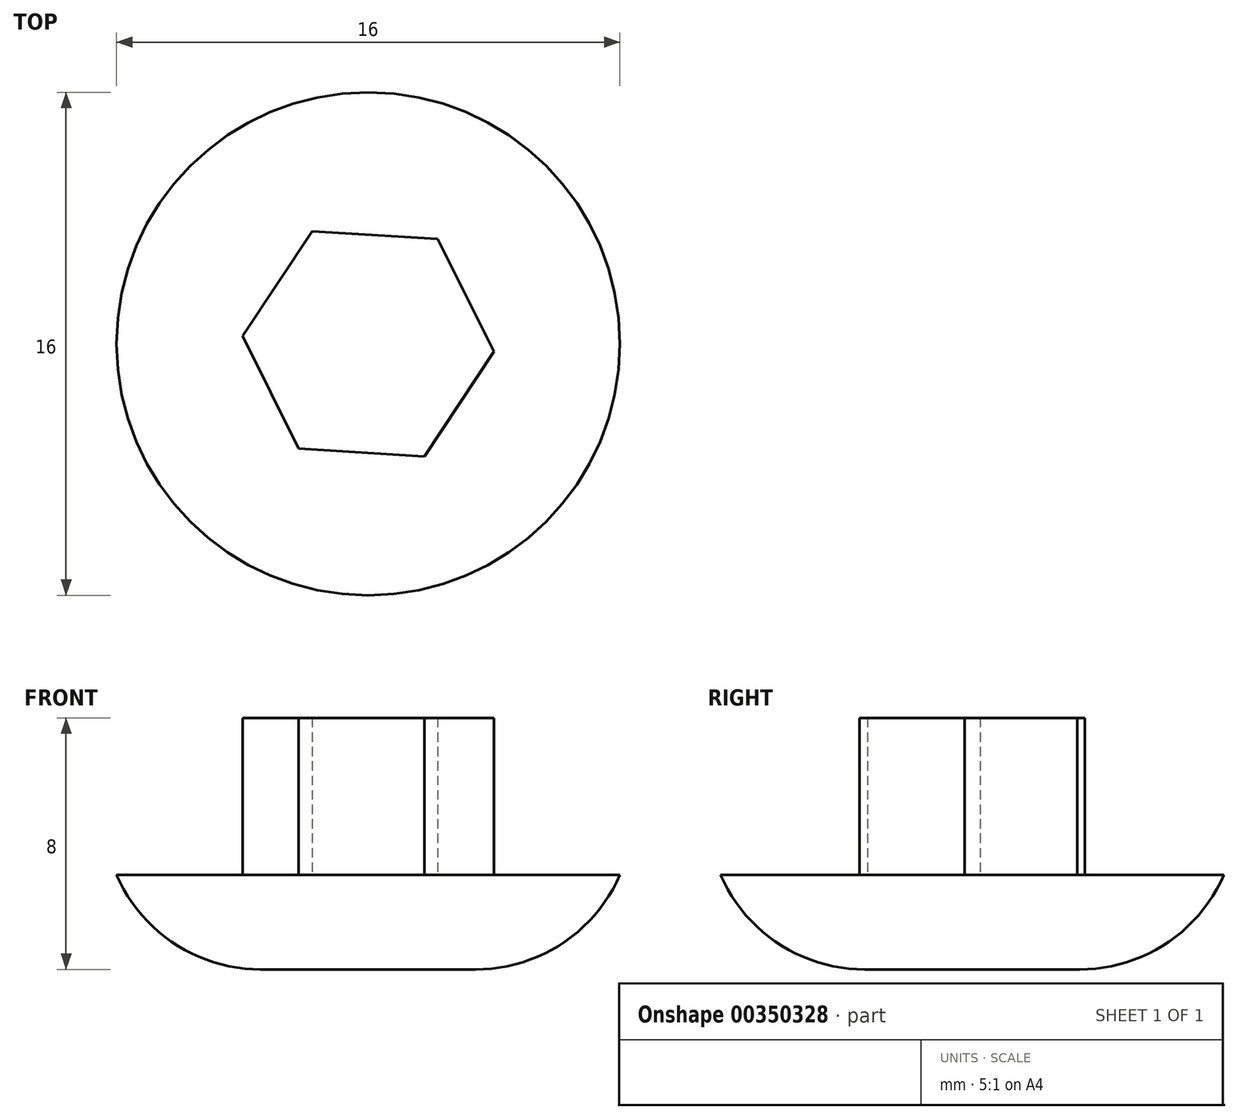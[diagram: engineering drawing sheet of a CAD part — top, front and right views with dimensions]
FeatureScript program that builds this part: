
annotation { "Feature Type Name" : "Feature", "Feature Type Description" : "" }
export const myFeature = defineFeature(function(context is Context, id is Id, definition is map)
    precondition{}
    {
        {
            var Q0;
            Q0=qCreatedBy(makeId("Top.planeOp"),FACE);
            var sketch = newSketch(context, id + "F0", { "sketchPlane" : qUnion([Q0])});
            skCircle(sketch, "E0.cCircle", {"center": v(0.6, 0) * mm, "radius": 3.46 * mm, "construction": true});
            skLineSegment(sketch, "E0.0", {"start": v(2.81, 3.33) * mm, "end": v(4.6, -0.25) * mm});
            skLineSegment(sketch, "E0.1", {"start": v(4.6, -0.25) * mm, "end": v(2.38, -3.58) * mm});
            skLineSegment(sketch, "E0.2", {"start": v(2.38, -3.58) * mm, "end": v(-1.61, -3.33) * mm});
            skLineSegment(sketch, "E0.3", {"start": v(-1.61, -3.33) * mm, "end": v(-3.4, 0.25) * mm});
            skLineSegment(sketch, "E0.4", {"start": v(-3.4, 0.25) * mm, "end": v(-1.18, 3.58) * mm});
            skLineSegment(sketch, "E0.5", {"start": v(-1.18, 3.58) * mm, "end": v(2.81, 3.33) * mm});
            skPoint(sketch, "E0.0.midPoint", {"position": v(3.7, 1.54) * mm});
            skSolve(sketch);
        }
        {
            var Q0;
            Q0=makeQuery(id+"F0.imprint","IMPRINT",FACE,{"disambiguationData":[TD([[makeQuery(id+"F0.imprint","IMPRINT",EDGE,{"derivedFrom":sQuery(id+"F0.wireOp",EDGE,"E0.0")}),-1.0]])]});
            extrude(context, id + "F1", {"entities" : qUnion([Q0]), "depth" : 5 * mm});
        }
        {
            var Q0;
            Q0=makeQuery(id+"F1.opExtrude","CAP_FACE",FACE,{"disambiguationData":[OSD([sQuery(id+"F0.wireOp",EDGE,"E0.0"),sQuery(id+"F0.wireOp",EDGE,"E0.1"),sQuery(id+"F0.wireOp",EDGE,"E0.2"),sQuery(id+"F0.wireOp",EDGE,"E0.3"),sQuery(id+"F0.wireOp",EDGE,"E0.4"),sQuery(id+"F0.wireOp",EDGE,"E0.5")])],"isStart":true});
            var sketch = newSketch(context, id + "F2", { "sketchPlane" : qUnion([Q0])});
            skLineSegment(sketch, "E1.0.0", {"start": v(-1.18, -3.58) * mm, "end": v(2.81, -3.33) * mm});
            skLineSegment(sketch, "E1.0.1", {"start": v(2.81, -3.33) * mm, "end": v(4.6, 0.25) * mm});
            skLineSegment(sketch, "E1.0.2", {"start": v(4.6, 0.25) * mm, "end": v(2.38, 3.58) * mm});
            skLineSegment(sketch, "E1.0.3", {"start": v(2.38, 3.58) * mm, "end": v(-1.61, 3.33) * mm});
            skLineSegment(sketch, "E1.0.4", {"start": v(-1.61, 3.33) * mm, "end": v(-3.4, -0.25) * mm});
            skLineSegment(sketch, "E1.0.5", {"start": v(-3.4, -0.25) * mm, "end": v(-1.18, -3.58) * mm});
            skLineSegment(sketch, "E2", {"start": v(-1.61, 3.33) * mm, "end": v(2.81, -3.33) * mm, "construction": true});
            skLineSegment(sketch, "E3", {"start": v(-1.18, -3.58) * mm, "end": v(2.38, 3.58) * mm, "construction": true});
            skLineSegment(sketch, "E4", {"start": v(4.6, 0.25) * mm, "end": v(-3.4, -0.25) * mm, "construction": true});
            skLineSegment(sketch, "E5", {"start": v(2.38, 3.58) * mm, "end": v(0.6, 0) * mm});
            skCircle(sketch, "E6", {"center": v(0.6, 0) * mm, "radius": 8 * mm});
            skSolve(sketch);
        }
        {
            var Q0;
            Q0=makeQuery(id+"F2.imprint","IMPRINT",FACE,{"disambiguationData":[TD([[makeQuery(id+"F2.imprint","IMPRINT",EDGE,{"derivedFrom":sQuery(id+"F2.wireOp",EDGE,"E1.0.0")}),-1.0]])]});
            var Q1;
            Q1=makeQuery(id+"F2.imprint","IMPRINT",FACE,{"disambiguationData":[TD([[makeQuery(id+"F2.imprint","IMPRINT",EDGE,{"derivedFrom":sQuery(id+"F2.wireOp",EDGE,"E1.0.0")}),1.0]])]});
            extrude(context, id + "F3", {"entities" : qUnion([Q0, Q1]), "operationType" : NewBodyOperationType.ADD, "depth" : 3 * mm});
        }
        {
            var Q0;
            Q0=makeQuery(id+"F3.opExtrude","CAP_FACE",FACE,{"disambiguationData":[OSD([sQuery(id+"F2.wireOp",EDGE,"E6")])],"isStart":false});
            fillet(context, id + "F4", {"entities" : qUnion([Q0]), "radius" : 5 * mm, "tangentPropagation" : true, "allowEdgeOverflow" : false});
        }
    });
